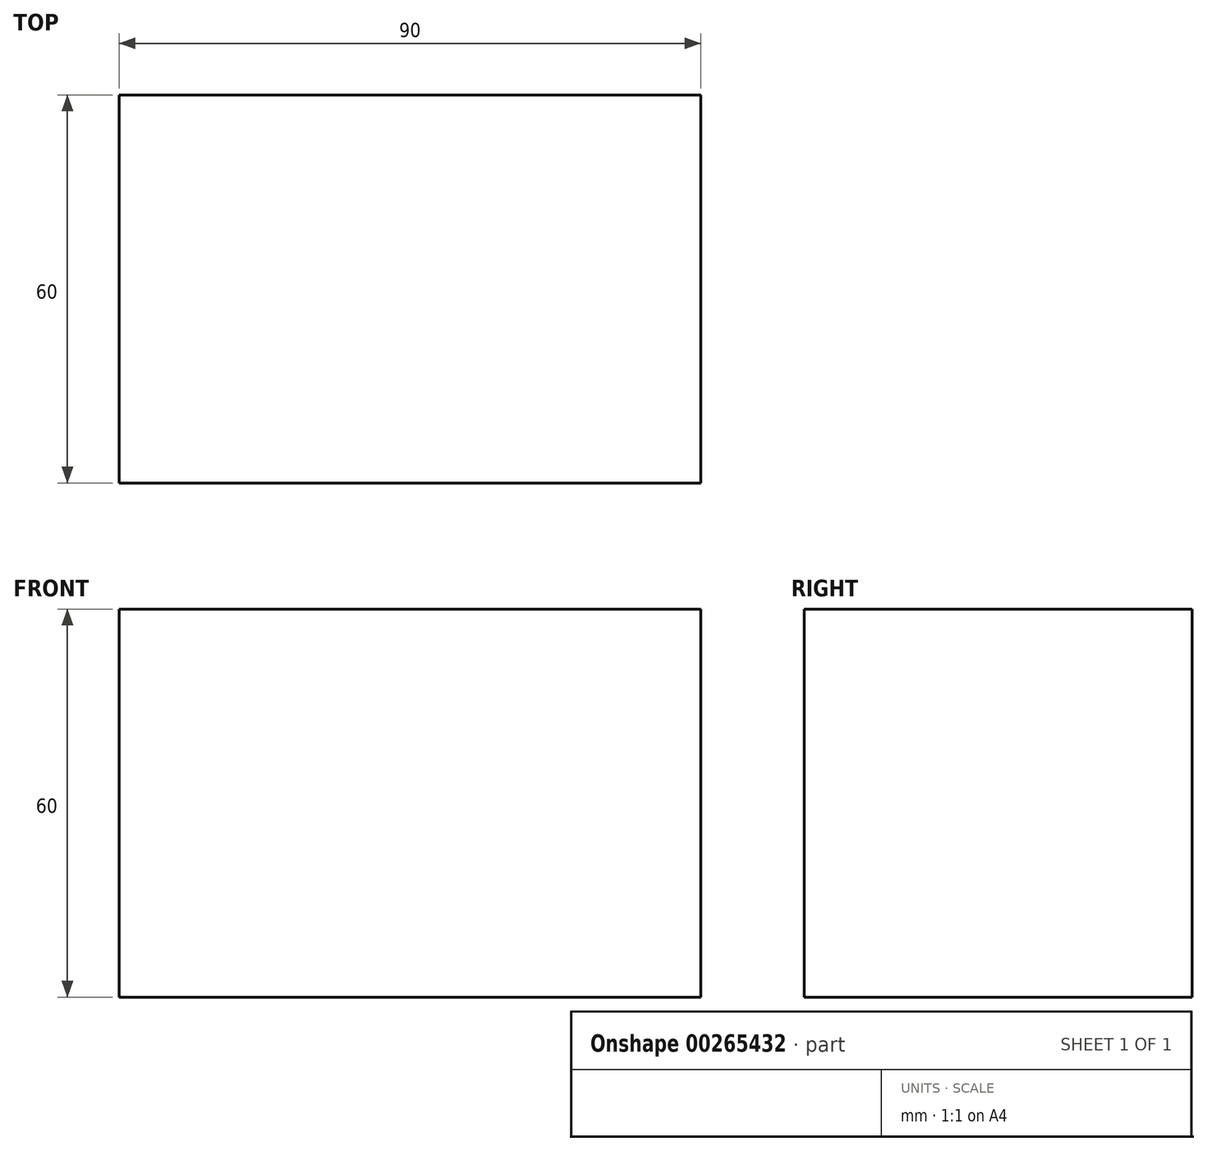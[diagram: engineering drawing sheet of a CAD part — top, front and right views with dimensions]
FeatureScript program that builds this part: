
annotation { "Feature Type Name" : "Feature", "Feature Type Description" : "" }
export const myFeature = defineFeature(function(context is Context, id is Id, definition is map)
    precondition{}
    {
        {
            var Q0;
            Q0=qCreatedBy(makeId("Front.planeOp"),FACE);
            var sketch = newSketch(context, id + "F0", { "sketchPlane" : qUnion([Q0])});
            skLineSegment(sketch, "E0.bottom", {"start": v(-45, 30) * mm, "end": v(45, 30) * mm});
            skLineSegment(sketch, "E0.top", {"start": v(-45, -30) * mm, "end": v(45, -30) * mm});
            skLineSegment(sketch, "E0.left", {"start": v(-45, 30) * mm, "end": v(-45, -30) * mm});
            skLineSegment(sketch, "E0.right", {"start": v(45, 30) * mm, "end": v(45, -30) * mm});
            skPoint(sketch, "E0.middle", {"position": v(0, 0) * mm});
            skSolve(sketch);
        }
        {
            var Q0;
            Q0=makeQuery(id+"F0.imprint","IMPRINT",FACE,{"disambiguationData":[TD([[makeQuery(id+"F0.imprint","IMPRINT",EDGE,{"derivedFrom":sQuery(id+"F0.wireOp",EDGE,"E0.bottom")}),-1.0]])]});
            extrude(context, id + "F1", {"entities" : qUnion([Q0]), "endBound" : BoundingType.SYMMETRIC, "depth" : 60 * mm});
        }
    });
